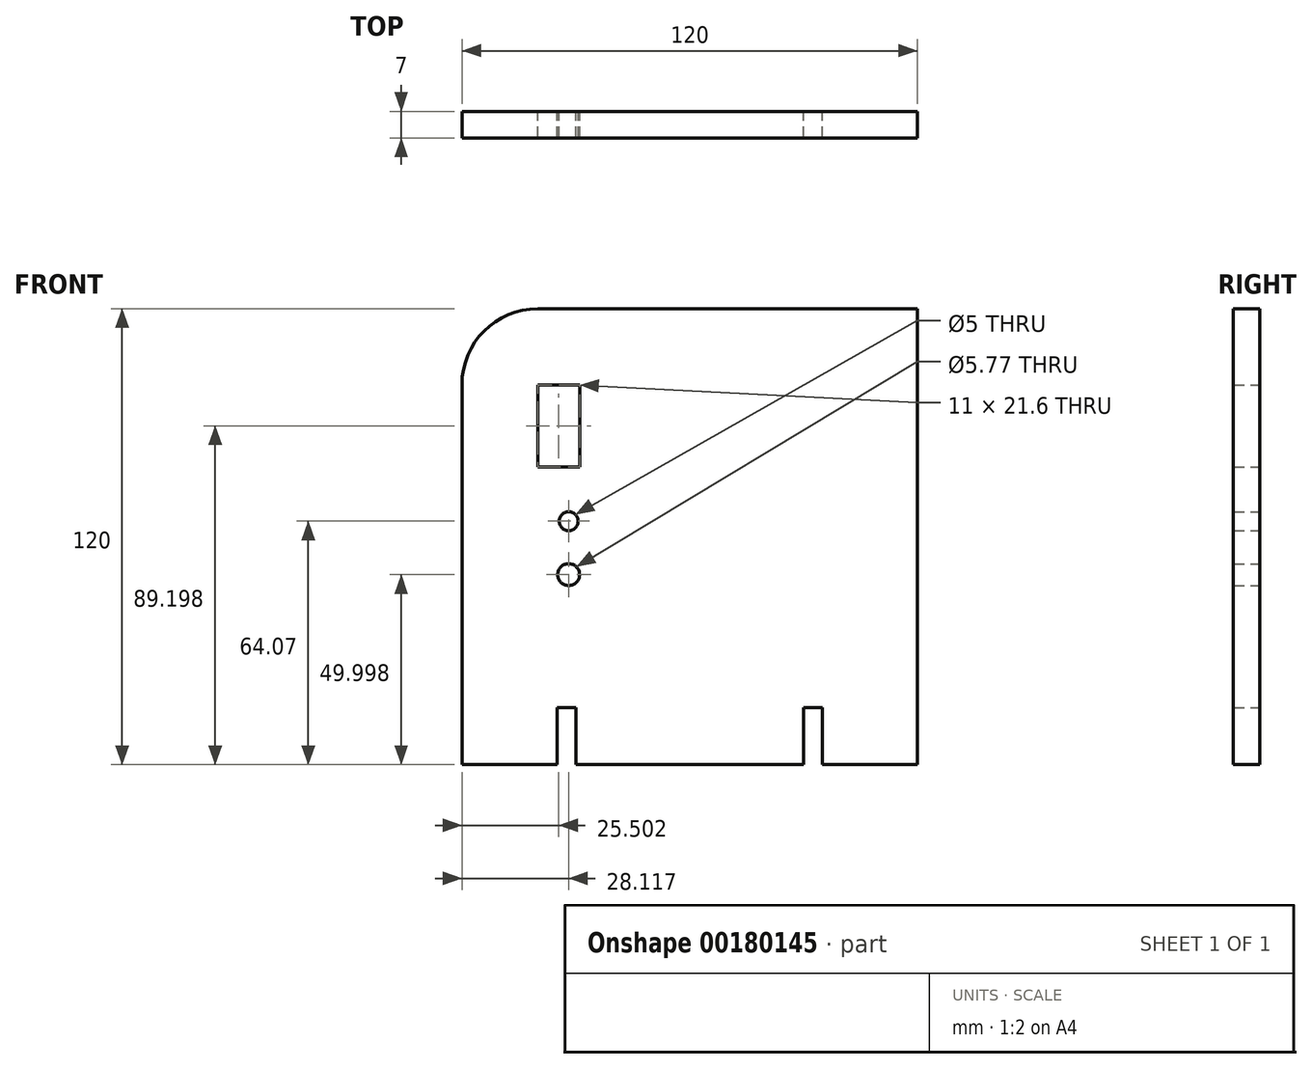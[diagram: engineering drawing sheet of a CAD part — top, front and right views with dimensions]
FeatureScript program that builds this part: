
annotation { "Feature Type Name" : "Feature", "Feature Type Description" : "" }
export const myFeature = defineFeature(function(context is Context, id is Id, definition is map)
    precondition{}
    {
        {
            var Q0;
            Q0=qCreatedBy(makeId("Front.planeOp"),FACE);
            var sketch = newSketch(context, id + "F0", { "sketchPlane" : qUnion([Q0])});
            skLineSegment(sketch, "E0", {"start": v(29.75, 66.69) * mm, "end": v(29.75, -53.31) * mm});
            skLineSegment(sketch, "E1", {"start": v(29.75, -53.31) * mm, "end": v(-90.25, -53.31) * mm});
            skLineSegment(sketch, "E2", {"start": v(-90.25, -53.31) * mm, "end": v(-90.25, 46.69) * mm});
            skLineSegment(sketch, "E3", {"start": v(-70.25, 66.69) * mm, "end": v(29.75, 66.69) * mm});
            skPoint(sketch, "E4.visualSharp", {"position": v(-90.25, 66.69) * mm});
            skArc(sketch, "E4.filletArc", {"start": v(-70.25, 66.69) * mm, "mid": v(-84.39, 60.83) * mm, "end": v(-90.25, 46.69) * mm});
            skLineSegment(sketch, "E5", {"start": v(-30.25, -53.31) * mm, "end": v(-30.25, -34.02) * mm, "construction": true});
            skLineSegment(sketch, "E6", {"start": v(-60.23, -53.31) * mm, "end": v(-60.23, -38.31) * mm});
            skLineSegment(sketch, "E7", {"start": v(-60.23, -38.31) * mm, "end": v(-65.23, -38.31) * mm});
            skLineSegment(sketch, "E8", {"start": v(-65.23, -38.31) * mm, "end": v(-65.23, -53.31) * mm});
            skLineSegment(sketch, "E9.MirrorCS", {"start": v(4.74, -38.31) * mm, "end": v(4.74, -53.31) * mm});
            skLineSegment(sketch, "E10.MirrorCS", {"start": v(-0.26, -38.31) * mm, "end": v(4.74, -38.31) * mm});
            skLineSegment(sketch, "E11.MirrorCS", {"start": v(-0.26, -53.31) * mm, "end": v(-0.26, -38.31) * mm});
            skLineSegment(sketch, "E12", {"start": v(-70.25, 46.69) * mm, "end": v(-70.25, 25.09) * mm});
            skLineSegment(sketch, "E13", {"start": v(-70.25, 25.09) * mm, "end": v(-59.25, 25.09) * mm});
            skLineSegment(sketch, "E14", {"start": v(-59.25, 25.09) * mm, "end": v(-59.25, 46.69) * mm});
            skLineSegment(sketch, "E15", {"start": v(-59.25, 46.69) * mm, "end": v(-70.25, 46.69) * mm});
            skCircle(sketch, "E16", {"center": v(-62.13, 10.76) * mm, "radius": 2.5 * mm});
            skCircle(sketch, "E17", {"center": v(-62.13, -3.31) * mm, "radius": 2.88 * mm});
            skPoint(sketch, "E17.centerSnap0", {"position": v(-90.25, -3.31) * mm});
            skSolve(sketch);
        }
        {
            var Q0;
            {var subQ2=sQuery(id+"F0.wireOp",EDGE,"E0");Q0=makeQuery(id+"F0.imprint","IMPRINT",FACE,{"disambiguationData":[TD([[makeQuery(id+"F0.imprint","IMPRINT",EDGE,{"derivedFrom":subQ2}),-1.0]])]});}
            extrude(context, id + "F1", {"entities" : qUnion([Q0]), "depth" : 7 * mm});
        }
    });
